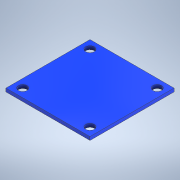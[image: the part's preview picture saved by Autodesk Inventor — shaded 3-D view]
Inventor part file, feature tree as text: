
AUTODESK INVENTOR PART (.ipt)
format: ipt  version: 2021 (Build 250183000, 183)  size: 113,152 bytes
history: native  units: mm
features: extrude x1, sketch x1
ambient origin geometry x8: Origin, YZ Plane, XZ Plane, XY Plane, X Axis, Y Axis, Z Axis, Center Point
bodies: Solid1 (feature_tree)
feature tree (2):
  extrude  "Extrusion1"  Depth=50.0mm
  sketch  "Sketch1"  dims[d0=50.0mm d1=50.0mm d2=40.0mm d3=40.0mm d4=5.1mm d5=5.1mm d6=5.1mm d7=5.1mm d8=2.0mm d9=0.0mm]
